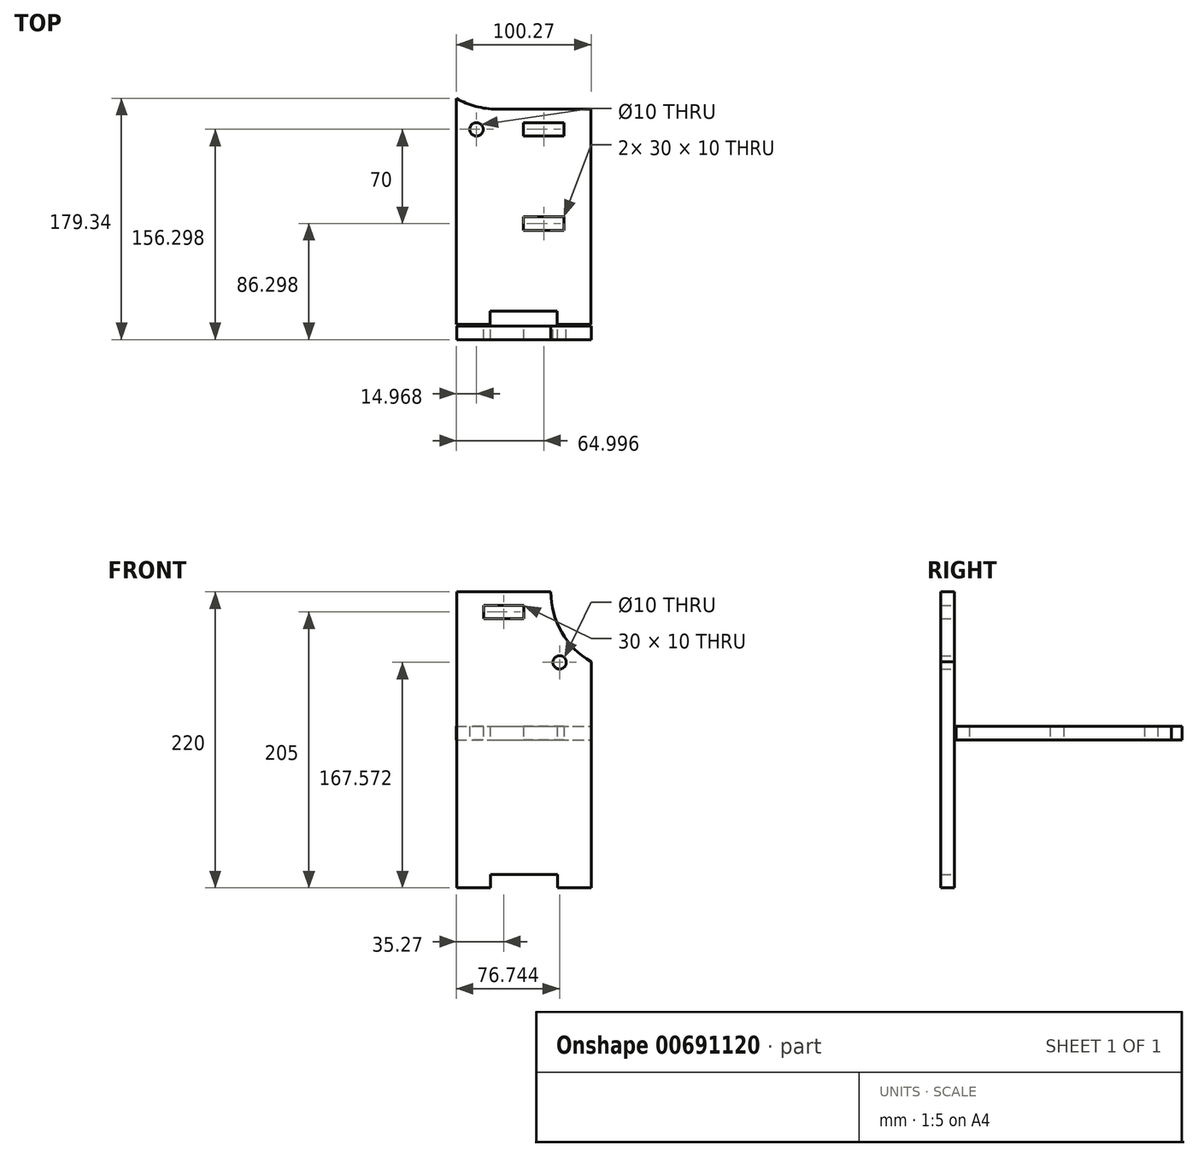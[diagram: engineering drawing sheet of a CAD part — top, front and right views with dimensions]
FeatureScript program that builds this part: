
annotation { "Feature Type Name" : "Feature", "Feature Type Description" : "" }
export const myFeature = defineFeature(function(context is Context, id is Id, definition is map)
    precondition{}
    {
        {
            var Q0;
            Q0=qCreatedBy(makeId("Front.planeOp"),FACE);
            var sketch = newSketch(context, id + "F0", { "sketchPlane" : qUnion([Q0])});
            skLineSegment(sketch, "E0.bottom", {"start": v(50, 110) * mm, "end": v(-50, 110) * mm});
            skLineSegment(sketch, "E0.top", {"start": v(50, -110) * mm, "end": v(-50, -110) * mm});
            skLineSegment(sketch, "E0.left", {"start": v(50, 110) * mm, "end": v(50, -110) * mm});
            skLineSegment(sketch, "E0.right", {"start": v(-50, 110) * mm, "end": v(-50, -110) * mm});
            skPoint(sketch, "E0.middle", {"position": v(0, 0) * mm});
            skLineSegment(sketch, "E1.bottom", {"start": v(0, 90) * mm, "end": v(-30, 90) * mm});
            skLineSegment(sketch, "E1.top", {"start": v(0, 100) * mm, "end": v(-30, 100) * mm});
            skLineSegment(sketch, "E1.left", {"start": v(0, 90) * mm, "end": v(0, 100) * mm});
            skLineSegment(sketch, "E1.right", {"start": v(-30, 90) * mm, "end": v(-30, 100) * mm});
            skPoint(sketch, "E1.middle", {"position": v(-15, 95) * mm});
            skArc(sketch, "E2", {"start": v(20, 110) * mm, "mid": v(28.04, 80) * mm, "end": v(50, 58.04) * mm});
            skCircle(sketch, "E3", {"center": v(26.47, 57.57) * mm, "radius": 5 * mm});
            skLineSegment(sketch, "E4.bottom", {"start": v(25, -110) * mm, "end": v(-25, -110) * mm});
            skLineSegment(sketch, "E4.top", {"start": v(25, -100) * mm, "end": v(-25, -100) * mm});
            skLineSegment(sketch, "E4.left", {"start": v(25, -110) * mm, "end": v(25, -100) * mm});
            skLineSegment(sketch, "E4.right", {"start": v(-25, -110) * mm, "end": v(-25, -100) * mm});
            skPoint(sketch, "E4.middle", {"position": v(0, -105) * mm});
            skLineSegment(sketch, "E5", {"start": v(50, 58.04) * mm, "end": v(50, -110) * mm});
            skSolve(sketch);
        }
        {
            var Q0;
            {var subQ3=sQuery(id+"F0.wireOp",EDGE,"vhTmC2f3-jtYe-idsq-PRUs-ck7xom4aEoTb");Q0=makeQuery(id+"F0.imprint","IMPRINT",FACE,{"disambiguationData":[TD([[makeQuery(id+"F0.imprint","IMPRINT",EDGE,{"derivedFrom":subQ3}),-1.0]])]});}
            var Q1;
            {var subQ1=sQuery(id+"F0.wireOp",EDGE,"E0.right");Q1=makeQuery(id+"F0.imprint","IMPRINT",FACE,{"disambiguationData":[TD([[makeQuery(id+"F0.imprint","IMPRINT",EDGE,{"derivedFrom":subQ1}),1.0]])]});}
            var Q2;
            {var subQ3=sQuery(id+"F0.wireOp",EDGE,"5geBSksE-TCDd-r9rk-HErB-lXMAxSbKvZ1L");Q2=makeQuery(id+"F0.imprint","IMPRINT",FACE,{"disambiguationData":[TD([[makeQuery(id+"F0.imprint","IMPRINT",EDGE,{"derivedFrom":subQ3}),1.0]])]});}
            var Q3;
            {var subQ1=sQuery(id+"F0.wireOp",EDGE,"E0.right");Q3=makeQuery(id+"F0.imprint","IMPRINT",FACE,{"disambiguationData":[TD([[makeQuery(id+"F0.imprint","IMPRINT",EDGE,{"derivedFrom":subQ1}),1.0]])]});}
            extrude(context, id + "F1", {"entities" : qUnion([Q0, Q1, Q2, Q3]), "depth" : 10 * mm, "offsetDistance" : 25 * mm});
        }
        {
            var Q0;
            Q0=qCreatedBy(makeId("Top.planeOp"),FACE);
            var sketch = newSketch(context, id + "F2", { "sketchPlane" : qUnion([Q0])});
            skLineSegment(sketch, "E6.left", {"start": v(-50.27, 221.3) * mm, "end": v(-50.27, 1.3) * mm});
            skLineSegment(sketch, "E7.MirrorCS", {"start": v(49.73, 221.3) * mm, "end": v(49.73, 1.3) * mm});
            skLineSegment(sketch, "E8.MirrorCS", {"start": v(-50.27, 221.3) * mm, "end": v(49.73, 221.3) * mm});
            skLineSegment(sketch, "E9.MirrorCS", {"start": v(-50.27, 1.3) * mm, "end": v(49.73, 1.3) * mm});
            skArc(sketch, "E10", {"start": v(-50.27, 169.34) * mm, "mid": v(-35.8, 163.34) * mm, "end": v(-20.27, 161.3) * mm});
            skLineSegment(sketch, "E11", {"start": v(-20.27, 161.3) * mm, "end": v(49.73, 161.3) * mm});
            skLineSegment(sketch, "E12.bottom", {"start": v(29.73, 141.3) * mm, "end": v(-0.27, 141.3) * mm});
            skLineSegment(sketch, "E12.top", {"start": v(29.73, 151.3) * mm, "end": v(-0.27, 151.3) * mm});
            skLineSegment(sketch, "E12.left", {"start": v(29.73, 141.3) * mm, "end": v(29.73, 151.3) * mm});
            skLineSegment(sketch, "E12.right", {"start": v(-0.27, 141.3) * mm, "end": v(-0.27, 151.3) * mm});
            skPoint(sketch, "E12.middle", {"position": v(14.73, 146.3) * mm});
            skCircle(sketch, "E13", {"center": v(-35.3, 146.3) * mm, "radius": 5 * mm});
            skLineSegment(sketch, "E14.MirrorCS", {"start": v(-25.27, 11.3) * mm, "end": v(24.73, 11.3) * mm});
            skLineSegment(sketch, "E15.MirrorCS", {"start": v(-25.27, 1.3) * mm, "end": v(-25.27, 11.3) * mm});
            skLineSegment(sketch, "E16.MirrorCS", {"start": v(24.73, 1.3) * mm, "end": v(24.73, 11.3) * mm});
            skLineSegment(sketch, "E17.MirrorCS", {"start": v(-25.27, 1.3) * mm, "end": v(24.73, 1.3) * mm});
            skLineSegment(sketch, "E18.MirrorCS", {"start": v(29.73, 81.3) * mm, "end": v(29.73, 71.3) * mm});
            skLineSegment(sketch, "E19.MirrorCS", {"start": v(-0.27, 81.3) * mm, "end": v(-0.27, 71.3) * mm});
            skLineSegment(sketch, "E20.MirrorCS", {"start": v(29.73, 71.3) * mm, "end": v(-0.27, 71.3) * mm});
            skLineSegment(sketch, "E21.MirrorCS", {"start": v(29.73, 81.3) * mm, "end": v(-0.27, 81.3) * mm});
            skLineSegment(sketch, "E22", {"start": v(-50.27, 169.34) * mm, "end": v(-50.27, 1.3) * mm});
            skSolve(sketch);
        }
        {
            var Q0;
            {var subQ1=sQuery(id+"F2.wireOp",EDGE,"E10");Q0=makeQuery(id+"F2.imprint","IMPRINT",FACE,{"disambiguationData":[TD([[makeQuery(id+"F2.imprint","IMPRINT",EDGE,{"derivedFrom":subQ1}),-1.0]])]});}
            extrude(context, id + "F3", {"entities" : qUnion([Q0]), "depth" : 10 * mm, "offsetDistance" : 25 * mm});
        }
    });
